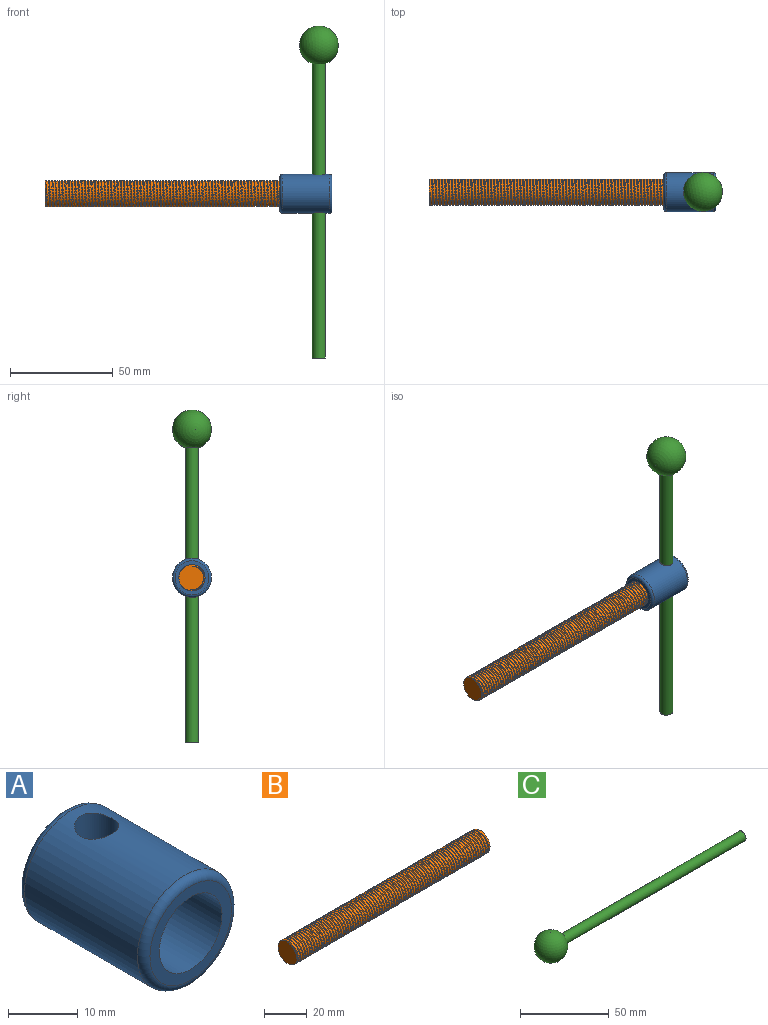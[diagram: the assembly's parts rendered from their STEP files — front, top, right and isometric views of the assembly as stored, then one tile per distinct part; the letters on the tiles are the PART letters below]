
ASSEMBLY  parts=3 mates=3
PART A: 8 faces, bbox 20.6x25.4x20.6 mm
  f0: cylinder r=9.53mm len=22.86mm, axis (0,1,0), area 1303.9mm2, adj f5,f6,f7
  f1: plane 16.51x16.51mm, normal (0,-1,0), area 87.4mm2, adj f3,f7
  f2: plane 16.51x16.51mm, normal (0,1,0), area 214.1mm2, adj f6
  f3: cylinder r=6.35mm len=12.7mm, axis (0,-1,0), area 506.7mm2, adj f1,f4
  f4: plane 12.7x12.7mm, normal (0,-1,0), area 126.7mm2, adj f3
  f5: cylinder r=3.17mm len=19.05mm, axis (0,0,1), area 369.2mm2, adj f0
  f6: torus R=8.26mm, axis (0,-1,0), area 113.6mm2, adj f0,f2
  f7: torus R=8.26mm, axis (0,-1,0), area 113.6mm2, adj f0,f1
PART B: 8 faces, bbox 127.7x14.7x12.8 mm
  f0: plane 12.78x12.78mm, normal (-1,0,0), area 123.8mm2, adj f1,f3,f4,f5
  f1: cylinder r=6.35mm len=127mm, axis (1,0,0), area 3369.4mm2, adj f0,f2,f3,f4,f6,f7
  f2: plane 12.78x12.78mm, normal (1,0,0), area 123.8mm2, adj f1,f5,f6,f7
  f3: plane 0.64x0.32mm, normal (0,-1,0), area 0.1mm2, adj f0,f1,f5,f7
  f4: bspline ~127.25x14.66mm, area 2067.6mm2, adj f0,f1,f5,f6
  f5: cylinder r=5.71mm len=127mm, axis (-1,0,0), area -291.7mm2, adj f0,f2,f3,f4,f6,f7
  f6: plane 0.64x0.32mm, normal (0,1,0), area 0.1mm2, adj f1,f2,f4,f5
  f7: bspline ~127.25x14.66mm, area 2077.8mm2, adj f1,f2,f3,f5
PART C: 3 faces, bbox 161.9x19.1x19.1 mm
  f0: cylinder r=3.17mm len=143.42mm, axis (-1,0,0), area 2861.1mm2, adj f1,f2
  f1: plane 6.35x6.35mm, normal (1,0,0), area 31.7mm2, adj f0
  f2: sphere r=9.53mm, area 1107.5mm2, adj f0
PLACE A rot(axis=(0,0,-1),90deg) t=(1.02,-3.67,-10.66)mm fixed
PLACE B rot(axis=(0,-0.01,1),0deg) t=(-11.68,-3.67,-10.66)mm
PLACE C rot(axis=(0.71,0.07,-0.71),172.2deg) t=(-5.33,-3.67,61.65)mm
MATE cylindrical C.f0 <-> A.f5  axis (0,0,1) through (-5.33,-3.67,-19.04)mm
MATE fastened B.f1 <-> A.f3  axis (1,0,0) through (-11.68,-3.67,-10.66)mm
MATE cylindrical B.f1 <-> A.f3  axis (1,0,0) through (-11.68,-3.67,-10.66)mm
